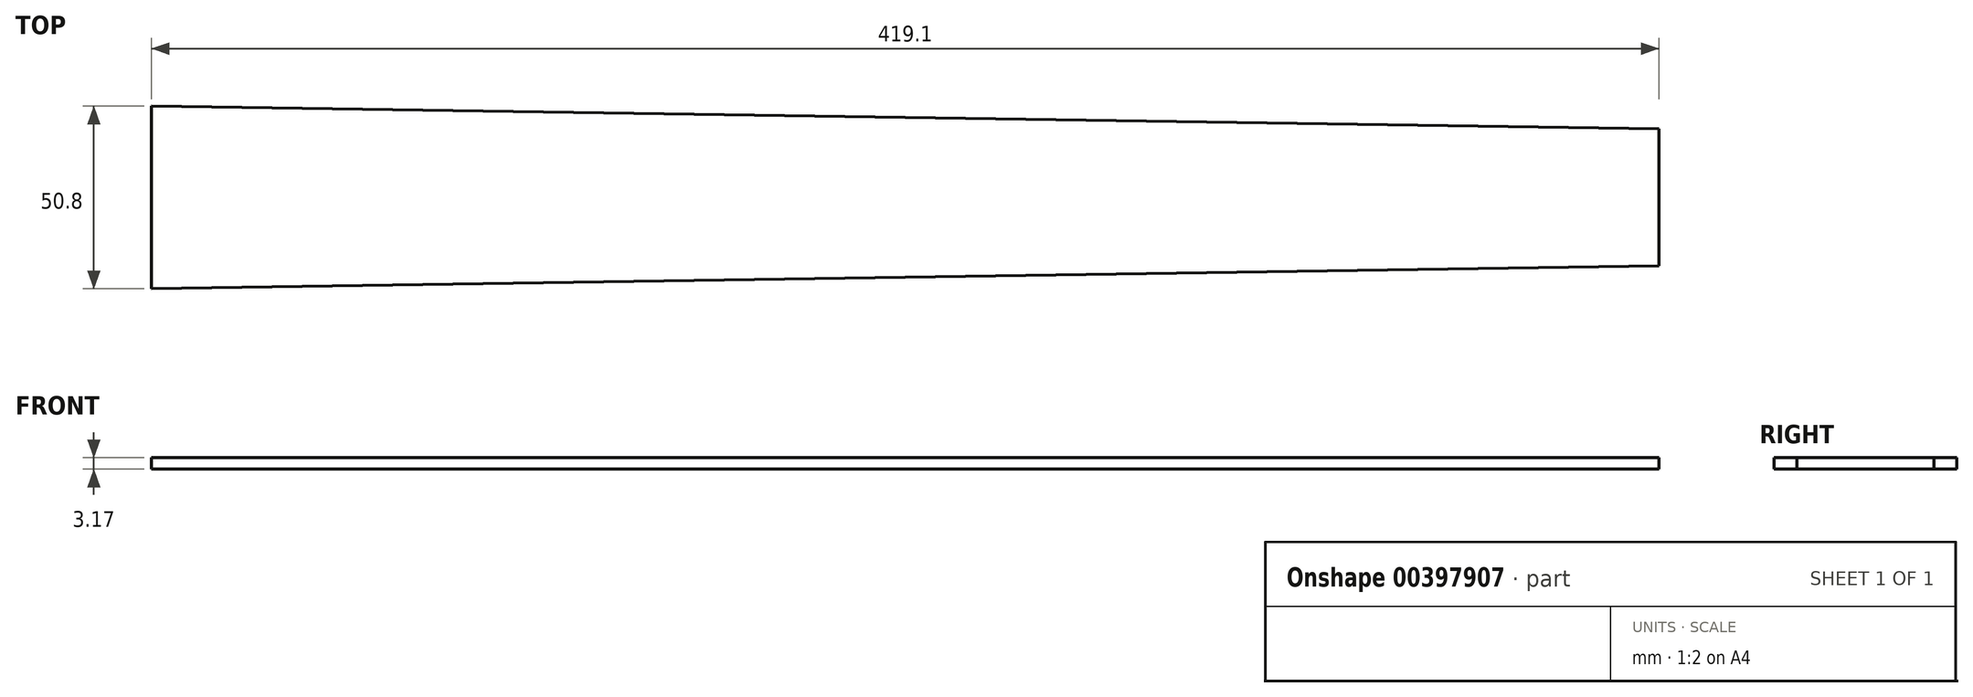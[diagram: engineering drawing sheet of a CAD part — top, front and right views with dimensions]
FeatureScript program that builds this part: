
annotation { "Feature Type Name" : "Feature", "Feature Type Description" : "" }
export const myFeature = defineFeature(function(context is Context, id is Id, definition is map)
    precondition{}
    {
        {
            var Q0;
            Q0=qCreatedBy(makeId("Top.planeOp"),FACE);
            var sketch = newSketch(context, id + "F0", { "sketchPlane" : qUnion([Q0])});
            skLineSegment(sketch, "E0.bottom", {"start": v(209.55, -25.4) * mm, "end": v(-209.55, -25.4) * mm, "construction": true});
            skLineSegment(sketch, "E0.top", {"start": v(209.55, 25.4) * mm, "end": v(-209.55, 25.4) * mm, "construction": true});
            skLineSegment(sketch, "E0.left", {"start": v(209.55, -25.4) * mm, "end": v(209.55, 25.4) * mm, "construction": true});
            skLineSegment(sketch, "E0.right", {"start": v(-209.55, -25.4) * mm, "end": v(-209.55, 25.4) * mm});
            skPoint(sketch, "E0.middle", {"position": v(0, 0) * mm});
            skLineSegment(sketch, "E1", {"start": v(-209.55, 0) * mm, "end": v(209.55, 0) * mm, "construction": true});
            skLineSegment(sketch, "E2", {"start": v(-209.55, 25.4) * mm, "end": v(209.55, 19.05) * mm});
            skLineSegment(sketch, "E3", {"start": v(209.55, 19.05) * mm, "end": v(209.55, -19.05) * mm});
            skLineSegment(sketch, "E4", {"start": v(209.55, -19.05) * mm, "end": v(-209.55, -25.4) * mm});
            skSolve(sketch);
        }
        {
            var Q0;
            Q0=makeQuery(id+"F0.imprint","IMPRINT",FACE,{"disambiguationData":[TD([[makeQuery(id+"F0.imprint","IMPRINT",EDGE,{"derivedFrom":sQuery(id+"F0.wireOp",EDGE,"E0.right")}),-1.0]])]});
            extrude(context, id + "F1", {"entities" : qUnion([Q0]), "depth" : 3.17 * mm});
        }
    });
